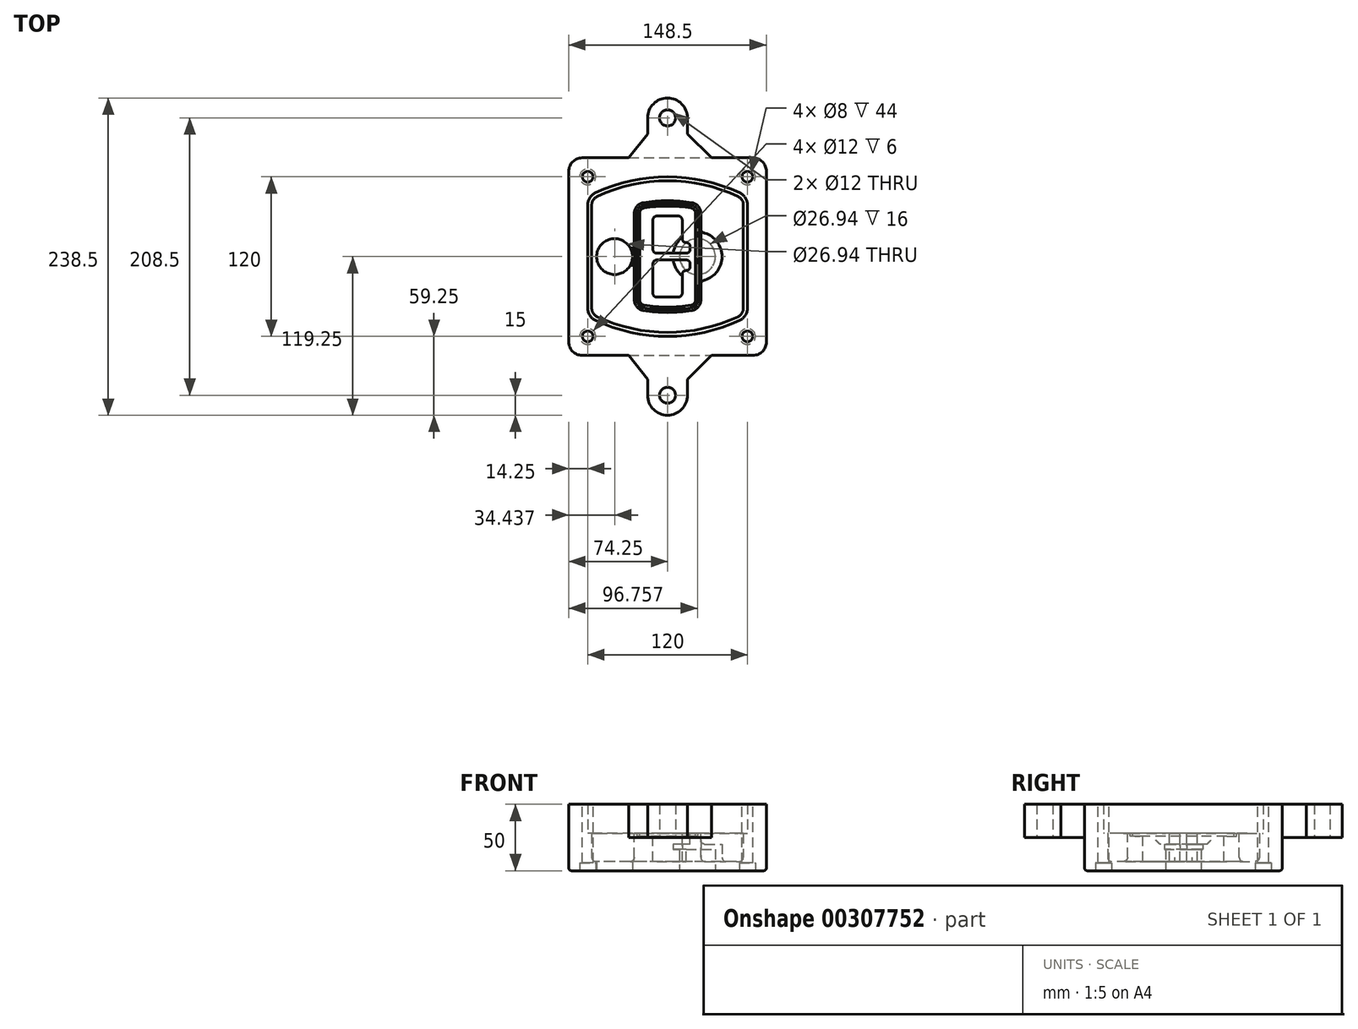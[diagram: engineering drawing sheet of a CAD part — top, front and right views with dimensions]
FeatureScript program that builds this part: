
annotation { "Feature Type Name" : "Feature", "Feature Type Description" : "" }
export const myFeature = defineFeature(function(context is Context, id is Id, definition is map)
    precondition{}
    {
        {
            var Q0;
            Q0=qCreatedBy(makeId("Top.planeOp"),FACE);
            var sketch = newSketch(context, id + "F0", { "sketchPlane" : qUnion([Q0])});
            skPoint(sketch, "E0.rect.middle", {"position": v(0, 0) * mm});
            skLineSegment(sketch, "E1.bottom", {"start": v(-64.25, -74.25) * mm, "end": v(64.25, -74.25) * mm});
            skLineSegment(sketch, "E1.top", {"start": v(-64.25, 74.25) * mm, "end": v(64.25, 74.25) * mm});
            skLineSegment(sketch, "E1.left", {"start": v(-74.25, -64.25) * mm, "end": v(-74.25, 64.25) * mm});
            skLineSegment(sketch, "E1.right", {"start": v(74.25, -64.25) * mm, "end": v(74.25, 64.25) * mm});
            skLineSegment(sketch, "E2", {"start": v(-74.25, 74.25) * mm, "end": v(74.25, -74.25) * mm, "construction": true});
            skLineSegment(sketch, "E3", {"start": v(74.25, 74.25) * mm, "end": v(-74.25, -74.25) * mm, "construction": true});
            skCircle(sketch, "E4", {"center": v(-60, 60) * mm, "radius": 4 * mm});
            skCircle(sketch, "E5", {"center": v(60, 60) * mm, "radius": 4 * mm});
            skCircle(sketch, "E6", {"center": v(60, -60) * mm, "radius": 4 * mm});
            skCircle(sketch, "E7", {"center": v(-60, -60) * mm, "radius": 4 * mm});
            skLineSegment(sketch, "E8", {"start": v(-60, 60) * mm, "end": v(60, 60) * mm, "construction": true});
            skLineSegment(sketch, "E9", {"start": v(60, 60) * mm, "end": v(60, -60) * mm, "construction": true});
            skLineSegment(sketch, "E10", {"start": v(60, -60) * mm, "end": v(-60, -60) * mm, "construction": true});
            skLineSegment(sketch, "E11", {"start": v(-60, -60) * mm, "end": v(-60, 60) * mm, "construction": true});
            skLineSegment(sketch, "E12", {"start": v(-60, 38.83) * mm, "end": v(-60, -38.83) * mm});
            skLineSegment(sketch, "E13", {"start": v(60, 38.83) * mm, "end": v(60, -38.83) * mm});
            skArc(sketch, "E14", {"start": v(54.26, 47.88) * mm, "mid": v(0, 60) * mm, "end": v(-54.26, 47.88) * mm});
            skArc(sketch, "E15", {"start": v(-54.26, -47.88) * mm, "mid": v(0, -60) * mm, "end": v(54.26, -47.88) * mm});
            skLineSegment(sketch, "E16", {"start": v(-60, 0) * mm, "end": v(60, 0) * mm, "construction": true});
            skPoint(sketch, "E17.visualSharp", {"position": v(-60, -45) * mm});
            skArc(sketch, "E17.filletArc", {"start": v(-60, -38.83) * mm, "mid": v(-58.44, -44.2) * mm, "end": v(-54.26, -47.88) * mm});
            skPoint(sketch, "E18.visualSharp", {"position": v(-60, 45) * mm});
            skArc(sketch, "E18.filletArc", {"start": v(-54.26, 47.88) * mm, "mid": v(-58.44, 44.2) * mm, "end": v(-60, 38.83) * mm});
            skPoint(sketch, "E19.visualSharp", {"position": v(60, 45) * mm});
            skArc(sketch, "E19.filletArc", {"start": v(60, 38.83) * mm, "mid": v(58.44, 44.2) * mm, "end": v(54.26, 47.88) * mm});
            skPoint(sketch, "E20.visualSharp", {"position": v(60, -45) * mm});
            skArc(sketch, "E20.filletArc", {"start": v(54.26, -47.88) * mm, "mid": v(58.44, -44.2) * mm, "end": v(60, -38.83) * mm});
            skPoint(sketch, "E21.visualSharp", {"position": v(-74.25, 74.25) * mm});
            skArc(sketch, "E21.filletArc", {"start": v(-64.25, 74.25) * mm, "mid": v(-71.32, 71.32) * mm, "end": v(-74.25, 64.25) * mm});
            skPoint(sketch, "E22.visualSharp", {"position": v(74.25, 74.25) * mm});
            skArc(sketch, "E22.filletArc", {"start": v(74.25, 64.25) * mm, "mid": v(71.32, 71.32) * mm, "end": v(64.25, 74.25) * mm});
            skPoint(sketch, "E23.visualSharp", {"position": v(74.25, -74.25) * mm});
            skArc(sketch, "E23.filletArc", {"start": v(64.25, -74.25) * mm, "mid": v(71.32, -71.32) * mm, "end": v(74.25, -64.25) * mm});
            skPoint(sketch, "E24.visualSharp", {"position": v(-74.25, -74.25) * mm});
            skArc(sketch, "E24.filletArc", {"start": v(-74.25, -64.25) * mm, "mid": v(-71.32, -71.32) * mm, "end": v(-64.25, -74.25) * mm});
            skArc(sketch, "E25.0", {"start": v(57, 38.83) * mm, "mid": v(55.9, 42.58) * mm, "end": v(52.98, 45.17) * mm});
            skLineSegment(sketch, "E25.1", {"start": v(57, 38.83) * mm, "end": v(57, -38.83) * mm});
            skArc(sketch, "E25.2", {"start": v(52.98, -45.17) * mm, "mid": v(55.9, -42.58) * mm, "end": v(57, -38.83) * mm});
            skArc(sketch, "E25.3", {"start": v(-52.98, -45.17) * mm, "mid": v(0, -57) * mm, "end": v(52.98, -45.17) * mm});
            skArc(sketch, "E25.4", {"start": v(-57, -38.83) * mm, "mid": v(-55.9, -42.58) * mm, "end": v(-52.98, -45.17) * mm});
            skArc(sketch, "E25.5", {"start": v(52.98, 45.17) * mm, "mid": v(0, 57) * mm, "end": v(-52.98, 45.17) * mm});
            skLineSegment(sketch, "E25.6", {"start": v(-57, 38.83) * mm, "end": v(-57, -38.83) * mm});
            skArc(sketch, "E25.7", {"start": v(-52.98, 45.17) * mm, "mid": v(-55.9, 42.58) * mm, "end": v(-57, 38.83) * mm});
            skArc(sketch, "E26.0", {"start": v(-55.96, 51.5) * mm, "mid": v(-61.82, 46.33) * mm, "end": v(-64, 38.83) * mm});
            skArc(sketch, "E26.1", {"start": v(55.96, 51.5) * mm, "mid": v(0, 64) * mm, "end": v(-55.96, 51.5) * mm});
            skArc(sketch, "E26.2", {"start": v(64, 38.83) * mm, "mid": v(61.82, 46.33) * mm, "end": v(55.96, 51.5) * mm});
            skLineSegment(sketch, "E26.3", {"start": v(64, 38.83) * mm, "end": v(64, -38.83) * mm});
            skArc(sketch, "E26.4", {"start": v(55.96, -51.5) * mm, "mid": v(61.82, -46.33) * mm, "end": v(64, -38.83) * mm});
            skLineSegment(sketch, "E26.5", {"start": v(-64, 38.83) * mm, "end": v(-64, -38.83) * mm});
            skArc(sketch, "E26.6", {"start": v(-55.96, -51.5) * mm, "mid": v(0, -64) * mm, "end": v(55.96, -51.5) * mm});
            skArc(sketch, "E26.7", {"start": v(-64, -38.83) * mm, "mid": v(-61.82, -46.33) * mm, "end": v(-55.96, -51.5) * mm});
            skSolve(sketch);
        }
        {
            var Q0;
            Q0=makeQuery(id+"F0.imprint","IMPRINT",FACE,{"disambiguationData":[TD([[makeQuery(id+"F0.imprint","IMPRINT",EDGE,{"derivedFrom":sQuery(id+"F0.wireOp",EDGE,"E1.bottom")}),1.0]])]});
            var Q1;
            Q1=makeQuery(id+"F0.imprint","IMPRINT",FACE,{"disambiguationData":[TD([[makeQuery(id+"F0.imprint","IMPRINT",EDGE,{"derivedFrom":sQuery(id+"F0.wireOp",EDGE,"E12")}),1.0]])]});
            var Q2;
            Q2=makeQuery(id+"F0.imprint","IMPRINT",FACE,{"disambiguationData":[TD([[makeQuery(id+"F0.imprint","IMPRINT",EDGE,{"derivedFrom":sQuery(id+"F0.wireOp",EDGE,"E25.0")}),1.0]])]});
            var Q3;
            Q3=makeQuery(id+"F0.imprint","IMPRINT",FACE,{"disambiguationData":[TD([[makeQuery(id+"F0.imprint","IMPRINT",EDGE,{"derivedFrom":sQuery(id+"F0.wireOp",EDGE,"E12")}),-1.0]])]});
            extrude(context, id + "F1", {"entities" : qUnion([Q0, Q1, Q2, Q3]), "oppositeDirection" : true, "depth" : 25 * mm});
        }
        {
            var Q0;
            Q0=makeQuery(id+"F0.imprint","IMPRINT",FACE,{"disambiguationData":[TD([[makeQuery(id+"F0.imprint","IMPRINT",EDGE,{"derivedFrom":sQuery(id+"F0.wireOp",EDGE,"E12")}),1.0]])]});
            extrude(context, id + "F2", {"entities" : qUnion([Q0]), "operationType" : NewBodyOperationType.ADD, "depth" : 3 * mm});
        }
        {
            var Q0;
            Q0=makeQuery(id+"F0.imprint","IMPRINT",FACE,{"disambiguationData":[TD([[makeQuery(id+"F0.imprint","IMPRINT",EDGE,{"derivedFrom":sQuery(id+"F0.wireOp",EDGE,"E25.0")}),1.0]])]});
            extrude(context, id + "F3", {"entities" : qUnion([Q0]), "operationType" : NewBodyOperationType.REMOVE, "oppositeDirection" : true, "depth" : 18 * mm});
        }
        {
            var Q0;
            Q0=makeQuery(id+"F2.opExtrude","CAP_FACE",FACE,{"disambiguationData":[OSD([sQuery(id+"F0.wireOp",EDGE,"E12"),sQuery(id+"F0.wireOp",EDGE,"E13"),sQuery(id+"F0.wireOp",EDGE,"E14"),sQuery(id+"F0.wireOp",EDGE,"E15"),sQuery(id+"F0.wireOp",EDGE,"E17.filletArc"),sQuery(id+"F0.wireOp",EDGE,"E18.filletArc"),sQuery(id+"F0.wireOp",EDGE,"E19.filletArc"),sQuery(id+"F0.wireOp",EDGE,"E20.filletArc"),sQuery(id+"F0.wireOp",EDGE,"E25.0"),sQuery(id+"F0.wireOp",EDGE,"E25.1"),sQuery(id+"F0.wireOp",EDGE,"E25.2"),sQuery(id+"F0.wireOp",EDGE,"E25.3"),sQuery(id+"F0.wireOp",EDGE,"E25.4"),sQuery(id+"F0.wireOp",EDGE,"E25.5"),sQuery(id+"F0.wireOp",EDGE,"E25.6"),sQuery(id+"F0.wireOp",EDGE,"E25.7")])],"isStart":false});
            var sketch = newSketch(context, id + "F4", { "sketchPlane" : qUnion([Q0])});
            skArc(sketch, "E27.0", {"start": v(-18.34, -40.45) * mm, "mid": v(0, -42) * mm, "end": v(18.34, -40.45) * mm});
            skArc(sketch, "E28.0", {"start": v(18.34, 40.45) * mm, "mid": v(0, 42) * mm, "end": v(-18.34, 40.45) * mm});
            skLineSegment(sketch, "E29", {"start": v(-25, 32.57) * mm, "end": v(-25, -32.57) * mm});
            skLineSegment(sketch, "E30", {"start": v(25, 32.57) * mm, "end": v(25, -32.57) * mm});
            skLineSegment(sketch, "E31", {"start": v(-25, 39.1) * mm, "end": v(25, 39.1) * mm, "construction": true});
            skLineSegment(sketch, "E32", {"start": v(-25, -39.1) * mm, "end": v(25, -39.1) * mm, "construction": true});
            skPoint(sketch, "E33.visualSharp", {"position": v(-25, 39.1) * mm});
            skArc(sketch, "E33.filletArc", {"start": v(-18.34, 40.45) * mm, "mid": v(-23.11, 37.73) * mm, "end": v(-25, 32.57) * mm});
            skPoint(sketch, "E34.visualSharp", {"position": v(25, 39.1) * mm});
            skArc(sketch, "E34.filletArc", {"start": v(25, 32.57) * mm, "mid": v(23.11, 37.73) * mm, "end": v(18.34, 40.45) * mm});
            skPoint(sketch, "E35.visualSharp", {"position": v(25, -39.1) * mm});
            skArc(sketch, "E35.filletArc", {"start": v(18.34, -40.45) * mm, "mid": v(23.11, -37.73) * mm, "end": v(25, -32.57) * mm});
            skPoint(sketch, "E36.visualSharp", {"position": v(-25, -39.1) * mm});
            skArc(sketch, "E36.filletArc", {"start": v(-25, -32.57) * mm, "mid": v(-23.11, -37.73) * mm, "end": v(-18.34, -40.45) * mm});
            skArc(sketch, "E37.0", {"start": v(52.98, 45.17) * mm, "mid": v(0, 57) * mm, "end": v(-52.98, 45.17) * mm});
            skArc(sketch, "E37.1", {"start": v(-52.98, 45.17) * mm, "mid": v(-55.9, 42.58) * mm, "end": v(-57, 38.83) * mm});
            skLineSegment(sketch, "E37.2", {"start": v(-57, 38.83) * mm, "end": v(-57, -38.83) * mm});
            skArc(sketch, "E37.3", {"start": v(-57, -38.83) * mm, "mid": v(-55.9, -42.58) * mm, "end": v(-52.98, -45.17) * mm});
            skArc(sketch, "E37.4", {"start": v(-52.98, -45.17) * mm, "mid": v(0, -57) * mm, "end": v(52.98, -45.17) * mm});
            skArc(sketch, "E37.5", {"start": v(52.98, -45.17) * mm, "mid": v(55.9, -42.58) * mm, "end": v(57, -38.83) * mm});
            skLineSegment(sketch, "E37.6", {"start": v(57, 38.83) * mm, "end": v(57, -38.83) * mm});
            skArc(sketch, "E37.7", {"start": v(57, 38.83) * mm, "mid": v(55.9, 42.58) * mm, "end": v(52.98, 45.17) * mm});
            skLineSegment(sketch, "E38.0", {"start": v(23, 32.57) * mm, "end": v(23, -32.57) * mm});
            skArc(sketch, "E38.1", {"start": v(18, -38.48) * mm, "mid": v(21.58, -36.44) * mm, "end": v(23, -32.57) * mm});
            skArc(sketch, "E38.2", {"start": v(-18, -38.48) * mm, "mid": v(0, -40) * mm, "end": v(18, -38.48) * mm});
            skArc(sketch, "E38.3", {"start": v(-23, -32.57) * mm, "mid": v(-21.58, -36.44) * mm, "end": v(-18, -38.48) * mm});
            skLineSegment(sketch, "E38.4", {"start": v(-23, 32.57) * mm, "end": v(-23, -32.57) * mm});
            skArc(sketch, "E38.5", {"start": v(23, 32.57) * mm, "mid": v(21.58, 36.44) * mm, "end": v(18, 38.48) * mm});
            skArc(sketch, "E38.6", {"start": v(-18, 38.48) * mm, "mid": v(-21.58, 36.44) * mm, "end": v(-23, 32.57) * mm});
            skArc(sketch, "E38.7", {"start": v(18, 38.48) * mm, "mid": v(0, 40) * mm, "end": v(-18, 38.48) * mm});
            skArc(sketch, "E39.0", {"start": v(21, 32.57) * mm, "mid": v(20.06, 35.15) * mm, "end": v(17.67, 36.5) * mm});
            skLineSegment(sketch, "E39.1", {"start": v(21, 32.57) * mm, "end": v(21, -32.57) * mm});
            skArc(sketch, "E39.2", {"start": v(17.67, -36.5) * mm, "mid": v(20.06, -35.15) * mm, "end": v(21, -32.57) * mm});
            skArc(sketch, "E39.3", {"start": v(-17.67, -36.5) * mm, "mid": v(0, -38) * mm, "end": v(17.67, -36.5) * mm});
            skArc(sketch, "E39.4", {"start": v(-21, -32.57) * mm, "mid": v(-20.06, -35.15) * mm, "end": v(-17.67, -36.5) * mm});
            skArc(sketch, "E39.5", {"start": v(17.67, 36.5) * mm, "mid": v(0, 38) * mm, "end": v(-17.67, 36.5) * mm});
            skLineSegment(sketch, "E39.6", {"start": v(-21, 32.57) * mm, "end": v(-21, -32.57) * mm});
            skArc(sketch, "E39.7", {"start": v(-17.67, 36.5) * mm, "mid": v(-20.06, 35.15) * mm, "end": v(-21, 32.57) * mm});
            skLineSegment(sketch, "E40", {"start": v(-25, 0) * mm, "end": v(25, 0) * mm, "construction": true});
            skLineSegment(sketch, "E41", {"start": v(-11, 5.5) * mm, "end": v(-11, 27.5) * mm});
            skLineSegment(sketch, "E42", {"start": v(-8, 30.5) * mm, "end": v(8, 30.5) * mm});
            skLineSegment(sketch, "E43", {"start": v(11, 27.5) * mm, "end": v(11, 13.5) * mm});
            skLineSegment(sketch, "E44", {"start": v(14, 10.5) * mm, "end": v(14, 10.5) * mm});
            skLineSegment(sketch, "E45", {"start": v(17, 7.5) * mm, "end": v(17, 5.5) * mm});
            skLineSegment(sketch, "E46", {"start": v(14, 2.5) * mm, "end": v(-8, 2.5) * mm});
            skPoint(sketch, "E47.visualSharp", {"position": v(-11, 30.5) * mm});
            skArc(sketch, "E47.filletArc", {"start": v(-8, 30.5) * mm, "mid": v(-10.12, 29.62) * mm, "end": v(-11, 27.5) * mm});
            skPoint(sketch, "E48.visualSharp", {"position": v(11, 30.5) * mm});
            skArc(sketch, "E48.filletArc", {"start": v(11, 27.5) * mm, "mid": v(10.12, 29.62) * mm, "end": v(8, 30.5) * mm});
            skPoint(sketch, "E49.visualSharp", {"position": v(11, 10.5) * mm});
            skArc(sketch, "E49.filletArc", {"start": v(11, 13.5) * mm, "mid": v(11.88, 11.38) * mm, "end": v(14, 10.5) * mm});
            skPoint(sketch, "E50.visualSharp", {"position": v(17, 10.5) * mm});
            skArc(sketch, "E50.filletArc", {"start": v(17, 7.5) * mm, "mid": v(16.12, 9.62) * mm, "end": v(14, 10.5) * mm});
            skPoint(sketch, "E51.visualSharp", {"position": v(17, 2.5) * mm});
            skArc(sketch, "E51.filletArc", {"start": v(14, 2.5) * mm, "mid": v(16.12, 3.38) * mm, "end": v(17, 5.5) * mm});
            skPoint(sketch, "E52.visualSharp", {"position": v(-11, 2.5) * mm});
            skArc(sketch, "E52.filletArc", {"start": v(-11, 5.5) * mm, "mid": v(-10.12, 3.38) * mm, "end": v(-8, 2.5) * mm});
            skLineSegment(sketch, "E53.0.MirrorCS", {"start": v(14, -2.5) * mm, "end": v(-8, -2.5) * mm});
            skArc(sketch, "E54.0.MirrorCS", {"start": v(-11, -5.5) * mm, "mid": v(-10.12, -3.38) * mm, "end": v(-8, -2.5) * mm});
            skLineSegment(sketch, "E55.0.MirrorCS", {"start": v(-11, -5.5) * mm, "end": v(-11, -27.5) * mm});
            skArc(sketch, "E56.0.MirrorCS", {"start": v(-8, -30.5) * mm, "mid": v(-10.12, -29.62) * mm, "end": v(-11, -27.5) * mm});
            skLineSegment(sketch, "E57.0.MirrorCS", {"start": v(-8, -30.5) * mm, "end": v(8, -30.5) * mm});
            skArc(sketch, "E58.0.MirrorCS", {"start": v(11, -27.5) * mm, "mid": v(10.12, -29.62) * mm, "end": v(8, -30.5) * mm});
            skLineSegment(sketch, "E59.0.MirrorCS", {"start": v(11, -27.5) * mm, "end": v(11, -13.5) * mm});
            skArc(sketch, "E60.0.MirrorCS", {"start": v(11, -13.5) * mm, "mid": v(11.88, -11.38) * mm, "end": v(14, -10.5) * mm});
            skArc(sketch, "E61.0.MirrorCS", {"start": v(17, -7.5) * mm, "mid": v(16.12, -9.62) * mm, "end": v(14, -10.5) * mm});
            skLineSegment(sketch, "E62.0.MirrorCS", {"start": v(17, -7.5) * mm, "end": v(17, -5.5) * mm});
            skArc(sketch, "E63.0.MirrorCS", {"start": v(14, -2.5) * mm, "mid": v(16.12, -3.38) * mm, "end": v(17, -5.5) * mm});
            skSolve(sketch);
        }
        {
            var Q0;
            Q0=makeQuery(id+"F4.imprint","IMPRINT",FACE,{"disambiguationData":[TD([[makeQuery(id+"F4.imprint","IMPRINT",EDGE,{"derivedFrom":sQuery(id+"F4.wireOp",EDGE,"E27.0")}),1.0]])]});
            var Q1;
            Q1=makeQuery(id+"F4.imprint","IMPRINT",FACE,{"disambiguationData":[TD([[makeQuery(id+"F4.imprint","IMPRINT",EDGE,{"derivedFrom":sQuery(id+"F4.wireOp",EDGE,"E38.0")}),-1.0]])]});
            var Q2;
            Q2=makeQuery(id+"F4.imprint","IMPRINT",FACE,{"disambiguationData":[TD([[makeQuery(id+"F4.imprint","IMPRINT",EDGE,{"derivedFrom":sQuery(id+"F4.wireOp",EDGE,"E39.0")}),1.0]])]});
            extrude(context, id + "F5", {"entities" : qUnion([Q0, Q1, Q2]), "operationType" : NewBodyOperationType.ADD, "endBound" : BoundingType.UP_TO_NEXT, "oppositeDirection" : true, "depth" : 25 * mm});
        }
        {
            var Q0;
            Q0=makeQuery(id+"F4.imprint","IMPRINT",FACE,{"disambiguationData":[TD([[makeQuery(id+"F4.imprint","IMPRINT",EDGE,{"derivedFrom":sQuery(id+"F4.wireOp",EDGE,"E38.0")}),-1.0]])]});
            extrude(context, id + "F6", {"entities" : qUnion([Q0]), "operationType" : NewBodyOperationType.REMOVE, "oppositeDirection" : true, "depth" : 2 * mm});
        }
        {
            var Q0;
            Q0=makeQuery(id+"F1.opExtrude","CAP_FACE",FACE,{"disambiguationData":[OSD([sQuery(id+"F0.wireOp",EDGE,"E1.bottom"),sQuery(id+"F0.wireOp",EDGE,"E1.top"),sQuery(id+"F0.wireOp",EDGE,"E1.left"),sQuery(id+"F0.wireOp",EDGE,"E1.right"),sQuery(id+"F0.wireOp",EDGE,"E4"),sQuery(id+"F0.wireOp",EDGE,"E5"),sQuery(id+"F0.wireOp",EDGE,"E6"),sQuery(id+"F0.wireOp",EDGE,"E7"),sQuery(id+"F0.wireOp",EDGE,"E21.filletArc"),sQuery(id+"F0.wireOp",EDGE,"E22.filletArc"),sQuery(id+"F0.wireOp",EDGE,"E23.filletArc"),sQuery(id+"F0.wireOp",EDGE,"E24.filletArc")])],"isStart":false});
            var sketch = newSketch(context, id + "F7", { "sketchPlane" : qUnion([Q0])});
            skCircle(sketch, "E64", {"center": v(22.5, 0) * mm, "radius": 13.47 * mm});
            skCircle(sketch, "E65", {"center": v(-39.81, 0) * mm, "radius": 13.47 * mm});
            skLineSegment(sketch, "E66", {"start": v(74.25, 0) * mm, "end": v(-74.25, 0) * mm});
            skCircle(sketch, "E67", {"center": v(22.5, 0) * mm, "radius": 18.47 * mm});
            skCircle(sketch, "E68", {"center": v(60, -60) * mm, "radius": 6 * mm});
            skCircle(sketch, "E69", {"center": v(-60, -60) * mm, "radius": 6 * mm});
            skCircle(sketch, "E70", {"center": v(-60, 60) * mm, "radius": 6 * mm});
            skCircle(sketch, "E71", {"center": v(60, 60) * mm, "radius": 6 * mm});
            skSolve(sketch);
        }
        {
            var Q0;
            {var subQ1=sQuery(id+"F7.wireOp",EDGE,"E66");var subQ4=sQuery(id+"F7.wireOp",EDGE,"E64");var subQ6=makeQuery(id+"F7.imprint","INTERSECT",VERTEX,{"disambiguationData":[OD(0.0)],"derivedFrom":[subQ4,subQ1]});Q0=makeQuery(id+"F7.imprint","IMPRINT",FACE,{"disambiguationData":[TD([[makeQuery(id+"F7.imprint","IMPRINT",EDGE,{"disambiguationData":[TD([[subQ6,-1.0]])],"derivedFrom":subQ4}),-1.0]])]});}
            var Q1;
            {var subQ0=sQuery(id+"F7.wireOp",EDGE,"E66");var subQ1=sQuery(id+"F7.wireOp",EDGE,"E64");var subQ3=makeQuery(id+"F7.imprint","INTERSECT",VERTEX,{"disambiguationData":[OD(0.0)],"derivedFrom":[subQ1,subQ0]});Q1=makeQuery(id+"F7.imprint","IMPRINT",FACE,{"disambiguationData":[TD([[makeQuery(id+"F7.imprint","IMPRINT",EDGE,{"disambiguationData":[TD([[subQ3,-1.0]])],"derivedFrom":subQ1}),1.0]])]});}
            var Q2;
            {var subQ0=sQuery(id+"F7.wireOp",EDGE,"E66");var subQ1=sQuery(id+"F7.wireOp",EDGE,"E64");var subQ3=makeQuery(id+"F7.imprint","INTERSECT",VERTEX,{"disambiguationData":[OD(0.0)],"derivedFrom":[subQ1,subQ0]});Q2=makeQuery(id+"F7.imprint","IMPRINT",FACE,{"disambiguationData":[TD([[makeQuery(id+"F7.imprint","IMPRINT",EDGE,{"disambiguationData":[TD([[subQ3,1.0]])],"derivedFrom":subQ1}),1.0]])]});}
            var Q3;
            {var subQ1=sQuery(id+"F7.wireOp",EDGE,"E66");var subQ4=sQuery(id+"F7.wireOp",EDGE,"E64");var subQ6=makeQuery(id+"F7.imprint","INTERSECT",VERTEX,{"disambiguationData":[OD(0.0)],"derivedFrom":[subQ4,subQ1]});Q3=makeQuery(id+"F7.imprint","IMPRINT",FACE,{"disambiguationData":[TD([[makeQuery(id+"F7.imprint","IMPRINT",EDGE,{"disambiguationData":[TD([[subQ6,1.0]])],"derivedFrom":subQ4}),-1.0]])]});}
            extrude(context, id + "F8", {"entities" : qUnion([Q0, Q1, Q2, Q3]), "operationType" : NewBodyOperationType.ADD, "oppositeDirection" : true, "depth" : 20 * mm});
        }
        {
            var Q0;
            {var subQ0=sQuery(id+"F7.wireOp",EDGE,"E66");var subQ1=sQuery(id+"F7.wireOp",EDGE,"E64");var subQ3=makeQuery(id+"F7.imprint","INTERSECT",VERTEX,{"disambiguationData":[OD(0.0)],"derivedFrom":[subQ1,subQ0]});Q0=makeQuery(id+"F7.imprint","IMPRINT",FACE,{"disambiguationData":[TD([[makeQuery(id+"F7.imprint","IMPRINT",EDGE,{"disambiguationData":[TD([[subQ3,-1.0]])],"derivedFrom":subQ1}),1.0]])]});}
            var Q1;
            {var subQ0=sQuery(id+"F7.wireOp",EDGE,"E66");var subQ1=sQuery(id+"F7.wireOp",EDGE,"E64");var subQ3=makeQuery(id+"F7.imprint","INTERSECT",VERTEX,{"disambiguationData":[OD(0.0)],"derivedFrom":[subQ1,subQ0]});Q1=makeQuery(id+"F7.imprint","IMPRINT",FACE,{"disambiguationData":[TD([[makeQuery(id+"F7.imprint","IMPRINT",EDGE,{"disambiguationData":[TD([[subQ3,1.0]])],"derivedFrom":subQ1}),1.0]])]});}
            extrude(context, id + "F9", {"entities" : qUnion([Q0, Q1]), "operationType" : NewBodyOperationType.REMOVE, "oppositeDirection" : true, "depth" : 16 * mm});
        }
        {
            var Q0;
            {var subQ0=sQuery(id+"F7.wireOp",EDGE,"E66");var subQ1=sQuery(id+"F7.wireOp",EDGE,"E65");var subQ3=makeQuery(id+"F7.imprint","INTERSECT",VERTEX,{"disambiguationData":[OD(0.0)],"derivedFrom":[subQ1,subQ0]});Q0=makeQuery(id+"F7.imprint","IMPRINT",FACE,{"disambiguationData":[TD([[makeQuery(id+"F7.imprint","IMPRINT",EDGE,{"disambiguationData":[TD([[subQ3,-1.0]])],"derivedFrom":subQ1}),1.0]])]});}
            var Q1;
            {var subQ0=sQuery(id+"F7.wireOp",EDGE,"E66");var subQ1=sQuery(id+"F7.wireOp",EDGE,"E65");var subQ3=makeQuery(id+"F7.imprint","INTERSECT",VERTEX,{"disambiguationData":[OD(0.0)],"derivedFrom":[subQ1,subQ0]});Q1=makeQuery(id+"F7.imprint","IMPRINT",FACE,{"disambiguationData":[TD([[makeQuery(id+"F7.imprint","IMPRINT",EDGE,{"disambiguationData":[TD([[subQ3,1.0]])],"derivedFrom":subQ1}),1.0]])]});}
            extrude(context, id + "F10", {"entities" : qUnion([Q0, Q1]), "operationType" : NewBodyOperationType.REMOVE, "oppositeDirection" : true, "depth" : 25 * mm});
        }
        {
            var Q0;
            Q0=makeQuery(id+"F7.imprint","IMPRINT",FACE,{"disambiguationData":[TD([[makeQuery(id+"F7.imprint","IMPRINT",EDGE,{"derivedFrom":sQuery(id+"F7.wireOp",EDGE,"E68")}),1.0]])]});
            var Q1;
            Q1=makeQuery(id+"F7.imprint","IMPRINT",FACE,{"disambiguationData":[TD([[makeQuery(id+"F7.imprint","IMPRINT",EDGE,{"derivedFrom":makeQuery(id+"F1.opExtrude","CAP_EDGE",EDGE,{"disambiguationData":[OSD([sQuery(id+"F0.wireOp",EDGE,"E5")])],"isStart":false})}),-1.0]])]});
            var Q2;
            Q2=makeQuery(id+"F7.imprint","IMPRINT",FACE,{"disambiguationData":[TD([[makeQuery(id+"F7.imprint","IMPRINT",EDGE,{"derivedFrom":sQuery(id+"F7.wireOp",EDGE,"E69")}),1.0]])]});
            var Q3;
            Q3=makeQuery(id+"F7.imprint","IMPRINT",FACE,{"disambiguationData":[TD([[makeQuery(id+"F7.imprint","IMPRINT",EDGE,{"derivedFrom":makeQuery(id+"F1.opExtrude","CAP_EDGE",EDGE,{"disambiguationData":[OSD([sQuery(id+"F0.wireOp",EDGE,"E4")])],"isStart":false})}),-1.0]])]});
            var Q4;
            Q4=makeQuery(id+"F7.imprint","IMPRINT",FACE,{"disambiguationData":[TD([[makeQuery(id+"F7.imprint","IMPRINT",EDGE,{"derivedFrom":sQuery(id+"F7.wireOp",EDGE,"E70")}),1.0]])]});
            var Q5;
            Q5=makeQuery(id+"F7.imprint","IMPRINT",FACE,{"disambiguationData":[TD([[makeQuery(id+"F7.imprint","IMPRINT",EDGE,{"derivedFrom":makeQuery(id+"F1.opExtrude","CAP_EDGE",EDGE,{"disambiguationData":[OSD([sQuery(id+"F0.wireOp",EDGE,"E7")])],"isStart":false})}),-1.0]])]});
            var Q6;
            Q6=makeQuery(id+"F7.imprint","IMPRINT",FACE,{"disambiguationData":[TD([[makeQuery(id+"F7.imprint","IMPRINT",EDGE,{"derivedFrom":sQuery(id+"F7.wireOp",EDGE,"E71")}),1.0]])]});
            var Q7;
            Q7=makeQuery(id+"F7.imprint","IMPRINT",FACE,{"disambiguationData":[TD([[makeQuery(id+"F7.imprint","IMPRINT",EDGE,{"derivedFrom":makeQuery(id+"F1.opExtrude","CAP_EDGE",EDGE,{"disambiguationData":[OSD([sQuery(id+"F0.wireOp",EDGE,"E6")])],"isStart":false})}),-1.0]])]});
            extrude(context, id + "F11", {"entities" : qUnion([Q0, Q1, Q2, Q3, Q4, Q5, Q6, Q7]), "operationType" : NewBodyOperationType.REMOVE, "oppositeDirection" : true, "depth" : 6 * mm});
        }
        {
            var Q0;
            Q0=makeQuery(id+"F9.boolean.opBoolean","COPY",FACE,{"derivedFrom":makeQuery(id+"F9.opExtrude","CAP_FACE",FACE,{"disambiguationData":[OSD([sQuery(id+"F7.wireOp",EDGE,"E64")])],"isStart":false})});
            var sketch = newSketch(context, id + "F12", { "sketchPlane" : qUnion([Q0])});
            skArc(sketch, "E72.0", {"start": v(11, 14.45) * mm, "mid": v(6.45, 9.13) * mm, "end": v(4.2, 2.5) * mm});
            skArc(sketch, "E72.1", {"start": v(4.2, -2.5) * mm, "mid": v(6.45, -9.13) * mm, "end": v(11, -14.45) * mm});
            skLineSegment(sketch, "E73", {"start": v(4.2, -2.5) * mm, "end": v(14, -2.5) * mm});
            skLineSegment(sketch, "E74.0", {"start": v(14, 2.5) * mm, "end": v(4.2, 2.5) * mm});
            skArc(sketch, "E74.1", {"start": v(14, 2.5) * mm, "mid": v(16.12, 3.38) * mm, "end": v(17, 5.5) * mm});
            skLineSegment(sketch, "E74.2", {"start": v(17, 7.5) * mm, "end": v(17, 5.5) * mm});
            skArc(sketch, "E74.3", {"start": v(17, 7.5) * mm, "mid": v(16.12, 9.62) * mm, "end": v(14, 10.5) * mm});
            skArc(sketch, "E74.4", {"start": v(11, 13.5) * mm, "mid": v(11.88, 11.38) * mm, "end": v(14, 10.5) * mm});
            skLineSegment(sketch, "E74.5", {"start": v(11, 14.45) * mm, "end": v(11, 13.5) * mm});
            skLineSegment(sketch, "E74.7", {"start": v(14, -2.5) * mm, "end": v(4.2, -2.5) * mm});
            skArc(sketch, "E74.8", {"start": v(14, -2.5) * mm, "mid": v(16.12, -3.38) * mm, "end": v(17, -5.5) * mm});
            skLineSegment(sketch, "E74.9", {"start": v(17, -7.5) * mm, "end": v(17, -5.5) * mm});
            skArc(sketch, "E74.10", {"start": v(17, -7.5) * mm, "mid": v(16.12, -9.62) * mm, "end": v(14, -10.5) * mm});
            skArc(sketch, "E74.11", {"start": v(11, -13.5) * mm, "mid": v(11.88, -11.38) * mm, "end": v(14, -10.5) * mm});
            skLineSegment(sketch, "E74.12", {"start": v(11, -14.45) * mm, "end": v(11, -13.5) * mm});
            skPoint(sketch, "E75.orphan", {"position": v(11, -27.5) * mm});
            skPoint(sketch, "E76.orphan", {"position": v(-8, -2.5) * mm});
            skPoint(sketch, "E77.orphan", {"position": v(-8, 2.5) * mm});
            skPoint(sketch, "E78.orphan", {"position": v(11, 27.5) * mm});
            skSolve(sketch);
        }
        {
            var Q0;
            {var subQ7=sQuery(id+"F12.wireOp",EDGE,"E72.0");var subQ14=sQuery(id+"F12.wireOp",EDGE,"E72.1");var subQ16=sQuery(id+"F12.wireOp",EDGE,"E74.1");var subQ18=sQuery(id+"F12.wireOp",EDGE,"E74.8");Q0=qUnion([makeQuery(id+"F12.imprint","IMPRINT",FACE,{"disambiguationData":[TD([[makeQuery(id+"F12.imprint","IMPRINT",EDGE,{"derivedFrom":subQ7}),1.0]])]}),makeQuery(id+"F12.imprint","IMPRINT",FACE,{"disambiguationData":[TD([[makeQuery(id+"F12.imprint","IMPRINT",EDGE,{"derivedFrom":subQ14}),1.0]])]}),makeQuery(id+"F12.imprint","IMPRINT",FACE,{"disambiguationData":[TD([[makeQuery(id+"F12.imprint","IMPRINT",EDGE,{"derivedFrom":subQ16}),1.0]])]}),makeQuery(id+"F12.imprint","IMPRINT",FACE,{"disambiguationData":[TD([[makeQuery(id+"F12.imprint","IMPRINT",EDGE,{"derivedFrom":subQ18}),-1.0]])]})]);}
            var Q1;
            Q1=makeQuery(id+"F5.boolean.opBoolean","SPLIT",FACE,{"disambiguationData":[TD([makeQuery(id+"F5.opExtrude","SWEPT_FACE",FACE,{"disambiguationData":[OSD([sQuery(id+"F4.wireOp",EDGE,"E41")])]})])],"derivedFrom":makeQuery(id+"F3.boolean.opBoolean","COPY",FACE,{"derivedFrom":makeQuery(id+"F3.opExtrude","CAP_FACE",FACE,{"disambiguationData":[OSD([sQuery(id+"F0.wireOp",EDGE,"E25.0"),sQuery(id+"F0.wireOp",EDGE,"E25.1"),sQuery(id+"F0.wireOp",EDGE,"E25.2"),sQuery(id+"F0.wireOp",EDGE,"E25.3"),sQuery(id+"F0.wireOp",EDGE,"E25.4"),sQuery(id+"F0.wireOp",EDGE,"E25.5"),sQuery(id+"F0.wireOp",EDGE,"E25.6"),sQuery(id+"F0.wireOp",EDGE,"E25.7")])],"isStart":false})})});
            extrude(context, id + "F13", {"entities" : qUnion([Q0]), "operationType" : NewBodyOperationType.REMOVE, "endBound" : BoundingType.UP_TO_SURFACE, "endBoundEntityFace" : qUnion([Q1]), "depth" : 25 * mm});
        }
        {
            var Q0;
            Q0=makeQuery(id+"F3.boolean.opBoolean","COPY",EDGE,{"derivedFrom":makeQuery(id+"F3.opExtrude","CAP_EDGE",EDGE,{"disambiguationData":[OSD([sQuery(id+"F0.wireOp",EDGE,"E25.6")])],"isStart":false})});
            var Q1;
            Q1=makeQuery(id+"F8.boolean.opBoolean","INTERSECT",EDGE,{"derivedFrom":[makeQuery(id+"F5.opExtrude","SWEPT_FACE",FACE,{"disambiguationData":[OSD([sQuery(id+"F4.wireOp",EDGE,"E30")])]}),makeQuery(id+"F8.opExtrude","CAP_FACE",FACE,{"disambiguationData":[OSD([sQuery(id+"F7.wireOp",EDGE,"E67")])],"isStart":false})]});
            var Q2;
            Q2=makeQuery(id+"F8.boolean.opBoolean","INTERSECT",EDGE,{"disambiguationData":[OD(1.0)],"derivedFrom":[makeQuery(id+"F5.opExtrude","SWEPT_FACE",FACE,{"disambiguationData":[OSD([sQuery(id+"F4.wireOp",EDGE,"E30")])]}),makeQuery(id+"F8.opExtrude","SWEPT_FACE",FACE,{"disambiguationData":[OSD([sQuery(id+"F7.wireOp",EDGE,"E67")])]})]});
            var Q3;
            {var subQ0=sQuery(id+"F4.wireOp",EDGE,"E30");Q3=makeQuery(id+"F8.boolean.opBoolean","SPLIT",EDGE,{"disambiguationData":[TD([makeQuery(id+"F5.opExtrude","SWEPT_FACE",FACE,{"disambiguationData":[OSD([sQuery(id+"F4.wireOp",EDGE,"E35.filletArc")])]})])],"derivedFrom":makeQuery(id+"F5.opExtrude","CAP_EDGE",EDGE,{"disambiguationData":[OSD([subQ0])],"isStart":false})});}
            var Q4;
            {var subQ0=sQuery(id+"F0.wireOp",EDGE,"E25.7");var subQ1=sQuery(id+"F0.wireOp",EDGE,"E25.1");var subQ2=sQuery(id+"F0.wireOp",EDGE,"E25.6");var subQ3=sQuery(id+"F0.wireOp",EDGE,"E25.5");var subQ4=sQuery(id+"F0.wireOp",EDGE,"E25.4");var subQ5=sQuery(id+"F0.wireOp",EDGE,"E25.0");var subQ6=sQuery(id+"F0.wireOp",EDGE,"E25.2");var subQ7=sQuery(id+"F0.wireOp",EDGE,"E25.3");Q4=makeQuery(id+"F8.boolean.opBoolean","INTERSECT",EDGE,{"derivedFrom":[makeQuery(id+"F5.boolean.opBoolean","SPLIT",FACE,{"disambiguationData":[TD([makeQuery(id+"F2.opExtrude","SWEPT_FACE",FACE,{"disambiguationData":[OSD([subQ5])]})])],"derivedFrom":makeQuery(id+"F3.boolean.opBoolean","COPY",FACE,{"derivedFrom":makeQuery(id+"F3.opExtrude","CAP_FACE",FACE,{"disambiguationData":[OSD([subQ5,subQ1,subQ6,subQ7,subQ4,subQ3,subQ2,subQ0])],"isStart":false})})}),makeQuery(id+"F8.opExtrude","SWEPT_FACE",FACE,{"disambiguationData":[OSD([sQuery(id+"F7.wireOp",EDGE,"E67")])]})]});}
            var Q5;
            Q5=makeQuery(id+"F8.boolean.opBoolean","INTERSECT",EDGE,{"disambiguationData":[OD(0.0)],"derivedFrom":[makeQuery(id+"F5.opExtrude","SWEPT_FACE",FACE,{"disambiguationData":[OSD([sQuery(id+"F4.wireOp",EDGE,"E30")])]}),makeQuery(id+"F8.opExtrude","SWEPT_FACE",FACE,{"disambiguationData":[OSD([sQuery(id+"F7.wireOp",EDGE,"E67")])]})]});
            fillet(context, id + "F14", {"entities" : qUnion([Q0, Q1, Q2, Q3, Q4, Q5]), "radius" : 3 * mm, "tangentPropagation" : true, "allowEdgeOverflow" : false});
        }
        {
            var Q0;
            Q0=makeQuery(id+"F1.opExtrude","CAP_EDGE",EDGE,{"disambiguationData":[OSD([sQuery(id+"F0.wireOp",EDGE,"E1.bottom")])],"isStart":false});
            fillet(context, id + "F15", {"entities" : qUnion([Q0]), "radius" : 2 * mm, "tangentPropagation" : true, "allowEdgeOverflow" : false});
        }
        {
            var Q0;
            {var subQ0=sQuery(id+"F0.wireOp",EDGE,"E21.filletArc");var subQ1=sQuery(id+"F0.wireOp",EDGE,"E7");var subQ2=sQuery(id+"F0.wireOp",EDGE,"E6");var subQ3=sQuery(id+"F0.wireOp",EDGE,"E5");var subQ4=sQuery(id+"F0.wireOp",EDGE,"E4");var subQ5=sQuery(id+"F0.wireOp",EDGE,"E22.filletArc");var subQ6=sQuery(id+"F0.wireOp",EDGE,"E1.bottom");var subQ7=sQuery(id+"F0.wireOp",EDGE,"E1.right");var subQ8=sQuery(id+"F0.wireOp",EDGE,"E1.top");var subQ9=sQuery(id+"F0.wireOp",EDGE,"E1.left");var subQ10=sQuery(id+"F0.wireOp",EDGE,"E23.filletArc");var subQ11=sQuery(id+"F0.wireOp",EDGE,"E24.filletArc");Q0=makeQuery(id+"F2.boolean.opBoolean","SPLIT",FACE,{"disambiguationData":[TD([makeQuery(id+"F1.opExtrude","SWEPT_FACE",FACE,{"disambiguationData":[OSD([subQ6])]})])],"derivedFrom":makeQuery(id+"F1.opExtrude","CAP_FACE",FACE,{"disambiguationData":[OSD([subQ6,subQ8,subQ9,subQ7,subQ4,subQ3,subQ2,subQ1,subQ0,subQ5,subQ10,subQ11])],"isStart":true})});}
            var sketch = newSketch(context, id + "F16", { "sketchPlane" : qUnion([Q0])});
            skCircle(sketch, "E79", {"center": v(0, 104.25) * mm, "radius": 6 * mm});
            skPoint(sketch, "E79.centerSnap0", {"position": v(0, 74.25) * mm});
            skArc(sketch, "E80", {"start": v(15, 104.25) * mm, "mid": v(0, 119.25) * mm, "end": v(-15, 104.25) * mm});
            skLineSegment(sketch, "E81", {"start": v(-15, 104.25) * mm, "end": v(-15, 92.25) * mm});
            skLineSegment(sketch, "E82", {"start": v(15, 104.25) * mm, "end": v(15, 92.25) * mm});
            skLineSegment(sketch, "E83", {"start": v(15, 92.25) * mm, "end": v(33, 74.25) * mm});
            skLineSegment(sketch, "E84", {"start": v(-15, 92.25) * mm, "end": v(-29.22, 74.25) * mm});
            skLineSegment(sketch, "E85", {"start": v(-86.42, 0) * mm, "end": v(97.75, 0) * mm, "construction": true});
            skPoint(sketch, "E85.startSnap0", {"position": v(-74.25, 0) * mm});
            skPoint(sketch, "E85.endSnap0", {"position": v(-74.25, 0) * mm});
            skLineSegment(sketch, "E86.MirrorCS", {"start": v(-15, -92.25) * mm, "end": v(-29.22, -74.25) * mm});
            skLineSegment(sketch, "E87.MirrorCS", {"start": v(-15, -104.25) * mm, "end": v(-15, -92.25) * mm});
            skLineSegment(sketch, "E88.MirrorCS", {"start": v(15, -92.25) * mm, "end": v(33, -74.25) * mm});
            skLineSegment(sketch, "E89.MirrorCS", {"start": v(15, -104.25) * mm, "end": v(15, -92.25) * mm});
            skArc(sketch, "E90.MirrorCS", {"start": v(15, -104.25) * mm, "mid": v(0, -119.25) * mm, "end": v(-15, -104.25) * mm});
            skCircle(sketch, "E91.MirrorC", {"center": v(0, -104.25) * mm, "radius": 6 * mm});
            skSolve(sketch);
        }
        {
            var Q0;
            Q0=makeQuery(id+"F16.imprint","IMPRINT",FACE,{"disambiguationData":[TD([[makeQuery(id+"F16.imprint","IMPRINT",EDGE,{"derivedFrom":sQuery(id+"F16.wireOp",EDGE,"E79")}),-1.0]])]});
            var Q1;
            {var subQ1=sQuery(id+"F16.wireOp",EDGE,"E86.MirrorCS");Q1=makeQuery(id+"F16.imprint","IMPRINT",FACE,{"disambiguationData":[TD([[makeQuery(id+"F16.imprint","IMPRINT",EDGE,{"derivedFrom":subQ1}),-1.0]])]});}
            var Q2;
            Q2=makeQuery(id+"F16.imprint","IMPRINT",FACE,{"disambiguationData":[TD([[makeQuery(id+"F16.imprint","IMPRINT",EDGE,{"derivedFrom":makeQuery(id+"F1.opExtrude","CAP_EDGE",EDGE,{"disambiguationData":[OSD([sQuery(id+"F0.wireOp",EDGE,"E1.left")])],"isStart":true})}),-1.0]])]});
            extrude(context, id + "F17", {"entities" : qUnion([Q0, Q1, Q2]), "operationType" : NewBodyOperationType.ADD, "depth" : 25 * mm});
        }
    });
